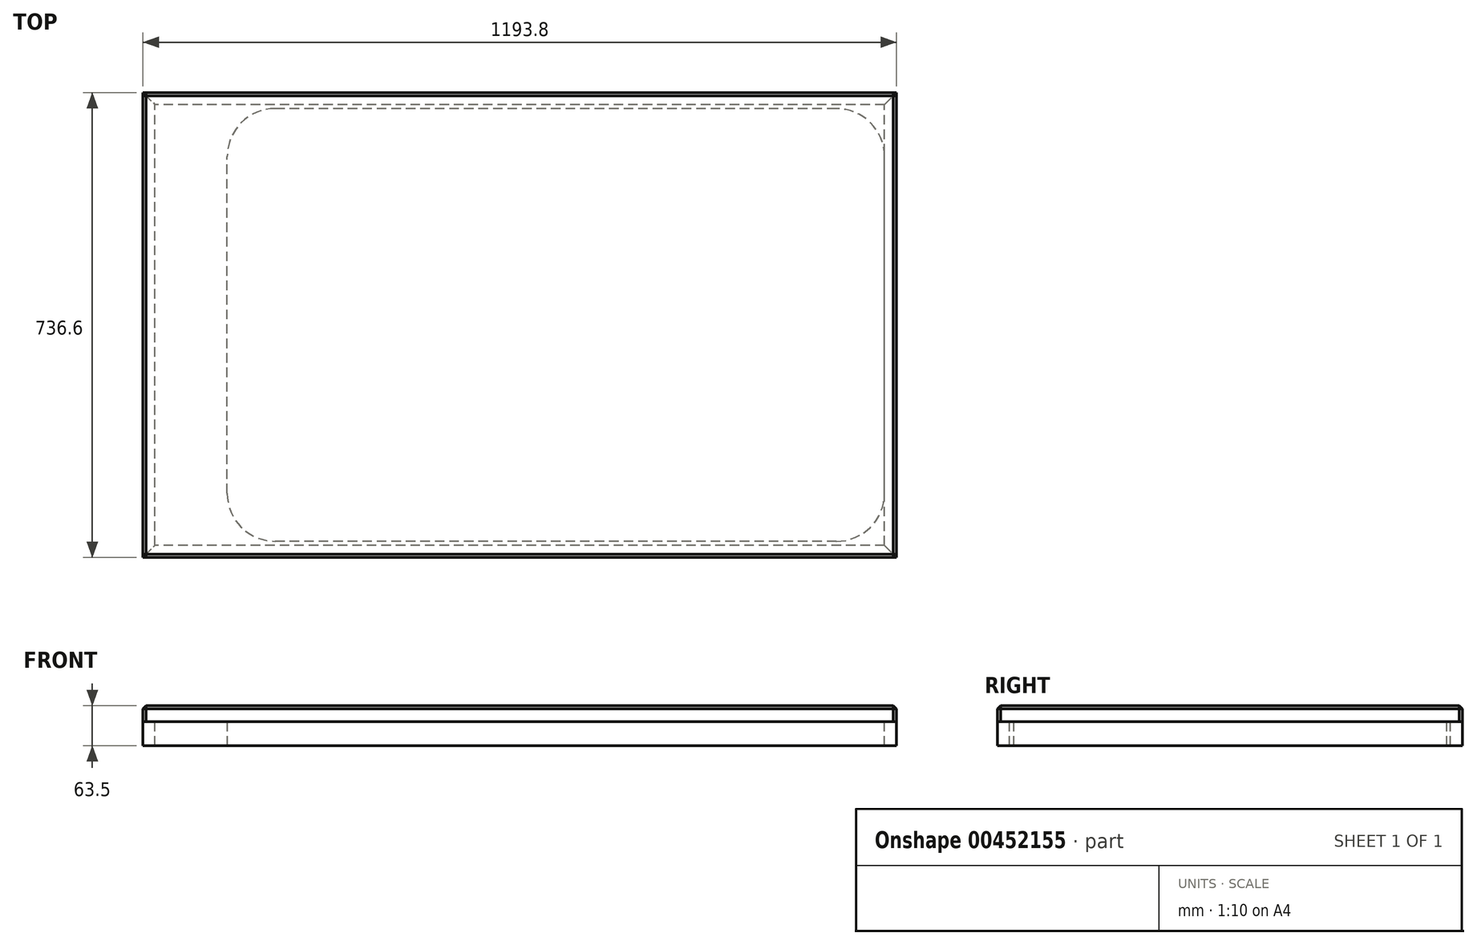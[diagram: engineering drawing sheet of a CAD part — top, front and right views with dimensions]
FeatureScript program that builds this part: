
annotation { "Feature Type Name" : "Feature", "Feature Type Description" : "" }
export const myFeature = defineFeature(function(context is Context, id is Id, definition is map)
    precondition{}
    {
        {
            var Q0;
            Q0=qCreatedBy(makeId("Top.planeOp"),FACE);
            var sketch = newSketch(context, id + "F0", { "sketchPlane" : qUnion([Q0])});
            skPoint(sketch, "E0.middle", {"position": v(0, 0) * mm});
            skLineSegment(sketch, "E1", {"start": v(-479.41, 0) * mm, "end": v(463.9, 0) * mm, "construction": true});
            skLineSegment(sketch, "E2.bottom", {"start": v(646.19, -342.9) * mm, "end": v(-242.81, -342.9) * mm});
            skLineSegment(sketch, "E2.top", {"start": v(646.19, 342.9) * mm, "end": v(-242.81, 342.9) * mm});
            skLineSegment(sketch, "E2.left", {"start": v(722.39, -266.7) * mm, "end": v(722.39, 266.7) * mm});
            skLineSegment(sketch, "E2.right", {"start": v(-319.01, -266.7) * mm, "end": v(-319.01, 266.7) * mm});
            skPoint(sketch, "E2.middle", {"position": v(201.69, 0) * mm});
            skPoint(sketch, "E3.visualSharp", {"position": v(-319.01, 342.9) * mm});
            skArc(sketch, "E3.filletArc", {"start": v(-242.81, 342.9) * mm, "mid": v(-296.7, 320.58) * mm, "end": v(-319.01, 266.7) * mm});
            skPoint(sketch, "E4.visualSharp", {"position": v(722.39, 342.9) * mm});
            skArc(sketch, "E4.filletArc", {"start": v(722.39, 266.7) * mm, "mid": v(700.07, 320.58) * mm, "end": v(646.19, 342.9) * mm});
            skPoint(sketch, "E5.visualSharp", {"position": v(722.39, -342.9) * mm});
            skArc(sketch, "E5.filletArc", {"start": v(646.19, -342.9) * mm, "mid": v(700.07, -320.58) * mm, "end": v(722.39, -266.7) * mm});
            skPoint(sketch, "E6.visualSharp", {"position": v(-319.01, -342.9) * mm});
            skArc(sketch, "E6.filletArc", {"start": v(-319.01, -266.7) * mm, "mid": v(-296.7, -320.58) * mm, "end": v(-242.81, -342.9) * mm});
            skSolve(sketch);
        }
        {
            var Q0;
            Q0=makeQuery(id+"F0.imprint","IMPRINT",FACE,{"disambiguationData":[TD([[makeQuery(id+"F0.imprint","IMPRINT",EDGE,{"derivedFrom":sQuery(id+"F0.wireOp",EDGE,"E2.bottom")}),-1.0]])]});
            extrude(context, id + "F1", {"entities" : qUnion([Q0]), "depth" : 38.1 * mm, "offsetDistance" : 25.4 * mm});
        }
        {
            var Q0;
            Q0=makeQuery(id+"F1.opExtrude","CAP_FACE",FACE,{"disambiguationData":[OSD([sQuery(id+"F0.wireOp",EDGE,"E2.bottom"),sQuery(id+"F0.wireOp",EDGE,"E2.top"),sQuery(id+"F0.wireOp",EDGE,"E2.left"),sQuery(id+"F0.wireOp",EDGE,"E2.right"),sQuery(id+"F0.wireOp",EDGE,"E3.filletArc"),sQuery(id+"F0.wireOp",EDGE,"E4.filletArc"),sQuery(id+"F0.wireOp",EDGE,"E5.filletArc"),sQuery(id+"F0.wireOp",EDGE,"E6.filletArc")])],"isStart":false});
            var sketch = newSketch(context, id + "F2", { "sketchPlane" : qUnion([Q0])});
            skLineSegment(sketch, "E7.bottom", {"start": v(741.44, -368.3) * mm, "end": v(-452.36, -368.3) * mm});
            skLineSegment(sketch, "E7.top", {"start": v(741.44, 368.3) * mm, "end": v(-452.36, 368.3) * mm});
            skLineSegment(sketch, "E7.left", {"start": v(741.44, -368.3) * mm, "end": v(741.44, 368.3) * mm});
            skLineSegment(sketch, "E7.right", {"start": v(-452.36, -368.3) * mm, "end": v(-452.36, 368.3) * mm});
            skPoint(sketch, "E7.middle", {"position": v(144.54, 0) * mm});
            skLineSegment(sketch, "E8.0", {"start": v(722.39, 349.25) * mm, "end": v(-433.31, 349.25) * mm});
            skLineSegment(sketch, "E8.1", {"start": v(722.39, -349.25) * mm, "end": v(722.39, 349.25) * mm});
            skLineSegment(sketch, "E8.2", {"start": v(722.39, -349.25) * mm, "end": v(-433.31, -349.25) * mm});
            skLineSegment(sketch, "E8.3", {"start": v(-433.31, -349.25) * mm, "end": v(-433.31, 349.25) * mm});
            skLineSegment(sketch, "E9", {"start": v(-452.36, 368.3) * mm, "end": v(-433.31, 349.25) * mm});
            skLineSegment(sketch, "E10", {"start": v(722.39, 349.25) * mm, "end": v(741.44, 368.3) * mm});
            skLineSegment(sketch, "E11", {"start": v(722.39, -349.25) * mm, "end": v(741.44, -368.3) * mm});
            skLineSegment(sketch, "E12", {"start": v(-452.36, -368.3) * mm, "end": v(-433.31, -349.25) * mm});
            skSolve(sketch);
        }
        {
            var Q0;
            Q0=makeQuery(id+"F2.imprint","IMPRINT",FACE,{"disambiguationData":[TD([[makeQuery(id+"F2.imprint","IMPRINT",EDGE,{"derivedFrom":sQuery(id+"F2.wireOp",EDGE,"E7.top")}),1.0]])]});
            var Q1;
            Q1=makeQuery(id+"F2.imprint","IMPRINT",FACE,{"disambiguationData":[TD([[makeQuery(id+"F2.imprint","IMPRINT",EDGE,{"derivedFrom":sQuery(id+"F2.wireOp",EDGE,"E7.bottom")}),-1.0]])]});
            extrude(context, id + "F3", {"entities" : qUnion([Q0, Q1]), "oppositeDirection" : true, "depth" : 38.1 * mm, "offsetDistance" : 25.4 * mm});
        }
        {
            var Q0;
            Q0=makeQuery(id+"F2.imprint","IMPRINT",FACE,{"disambiguationData":[TD([[makeQuery(id+"F2.imprint","IMPRINT",EDGE,{"derivedFrom":makeQuery(id+"F1.opExtrude","CAP_EDGE",EDGE,{"disambiguationData":[OSD([sQuery(id+"F0.wireOp",EDGE,"E2.bottom")])],"isStart":false})}),-1.0]])]});
            var Q1;
            Q1=makeQuery(id+"F2.imprint","IMPRINT",FACE,{"disambiguationData":[TD([[makeQuery(id+"F2.imprint","IMPRINT",EDGE,{"derivedFrom":sQuery(id+"F2.wireOp",EDGE,"E7.bottom")}),-1.0]])]});
            var Q2;
            Q2=makeQuery(id+"F2.imprint","IMPRINT",FACE,{"disambiguationData":[TD([[makeQuery(id+"F2.imprint","IMPRINT",EDGE,{"derivedFrom":sQuery(id+"F2.wireOp",EDGE,"E7.left")}),1.0]])]});
            var Q3;
            Q3=makeQuery(id+"F2.imprint","IMPRINT",FACE,{"disambiguationData":[TD([[makeQuery(id+"F2.imprint","IMPRINT",EDGE,{"derivedFrom":sQuery(id+"F2.wireOp",EDGE,"E7.right")}),-1.0]])]});
            var Q4;
            {var subQ0=sQuery(id+"F2.wireOp",EDGE,"E8.0");Q4=makeQuery(id+"F2.imprint","IMPRINT",FACE,{"disambiguationData":[TD([[makeQuery(id+"F2.imprint","IMPRINT",EDGE,{"derivedFrom":subQ0}),1.0]])]});}
            var Q5;
            Q5=makeQuery(id+"F2.imprint","IMPRINT",FACE,{"disambiguationData":[TD([[makeQuery(id+"F2.imprint","IMPRINT",EDGE,{"derivedFrom":sQuery(id+"F2.wireOp",EDGE,"E7.top")}),1.0]])]});
            extrude(context, id + "F4", {"entities" : qUnion([Q0, Q1, Q2, Q3, Q4, Q5]), "depth" : 25.4 * mm, "offsetDistance" : 25.4 * mm});
        }
        {
            var Q0;
            Q0=makeQuery(id+"F2.imprint","IMPRINT",FACE,{"disambiguationData":[TD([[makeQuery(id+"F2.imprint","IMPRINT",EDGE,{"derivedFrom":sQuery(id+"F2.wireOp",EDGE,"E7.right")}),-1.0]])]});
            var Q1;
            Q1=makeQuery(id+"F2.imprint","IMPRINT",FACE,{"disambiguationData":[TD([[makeQuery(id+"F2.imprint","IMPRINT",EDGE,{"derivedFrom":sQuery(id+"F2.wireOp",EDGE,"E7.left")}),1.0]])]});
            extrude(context, id + "F5", {"entities" : qUnion([Q0, Q1]), "oppositeDirection" : true, "depth" : 38.1 * mm, "offsetDistance" : 25.4 * mm});
        }
        {
            var Q0;
            Q0=makeQuery(id+"F4.opExtrude","CAP_FACE",FACE,{"disambiguationData":[OSD([sQuery(id+"F2.wireOp",EDGE,"E7.bottom"),sQuery(id+"F2.wireOp",EDGE,"E7.top"),sQuery(id+"F2.wireOp",EDGE,"E7.left"),sQuery(id+"F2.wireOp",EDGE,"E7.right")])],"isStart":false});
            var Q1;
            Q1=makeQuery(id+"F4.opExtrude","SWEPT_EDGE",EDGE,{"disambiguationData":[OSD([sQuery(id+"F2.wireOp",EDGE,"E7.bottom"),sQuery(id+"F2.wireOp",EDGE,"E7.left"),sQuery(id+"F2.wireOp",EDGE,"E11")])]});
            var Q2;
            Q2=makeQuery(id+"F4.opExtrude","SWEPT_EDGE",EDGE,{"disambiguationData":[OSD([sQuery(id+"F2.wireOp",EDGE,"E7.top"),sQuery(id+"F2.wireOp",EDGE,"E7.left"),sQuery(id+"F2.wireOp",EDGE,"E10")])]});
            var Q3;
            Q3=makeQuery(id+"F4.opExtrude","SWEPT_EDGE",EDGE,{"disambiguationData":[OSD([sQuery(id+"F2.wireOp",EDGE,"E7.bottom"),sQuery(id+"F2.wireOp",EDGE,"E7.right"),sQuery(id+"F2.wireOp",EDGE,"E12")])]});
            var Q4;
            Q4=makeQuery(id+"F4.opExtrude","SWEPT_EDGE",EDGE,{"disambiguationData":[OSD([sQuery(id+"F2.wireOp",EDGE,"E7.top"),sQuery(id+"F2.wireOp",EDGE,"E7.right"),sQuery(id+"F2.wireOp",EDGE,"E9")])]});
            chamfer(context, id + "F6", {"entities" : qUnion([Q0, Q1, Q2, Q3, Q4]), "width" : 5.08 * mm, "tangentPropagation" : true});
        }
    });
